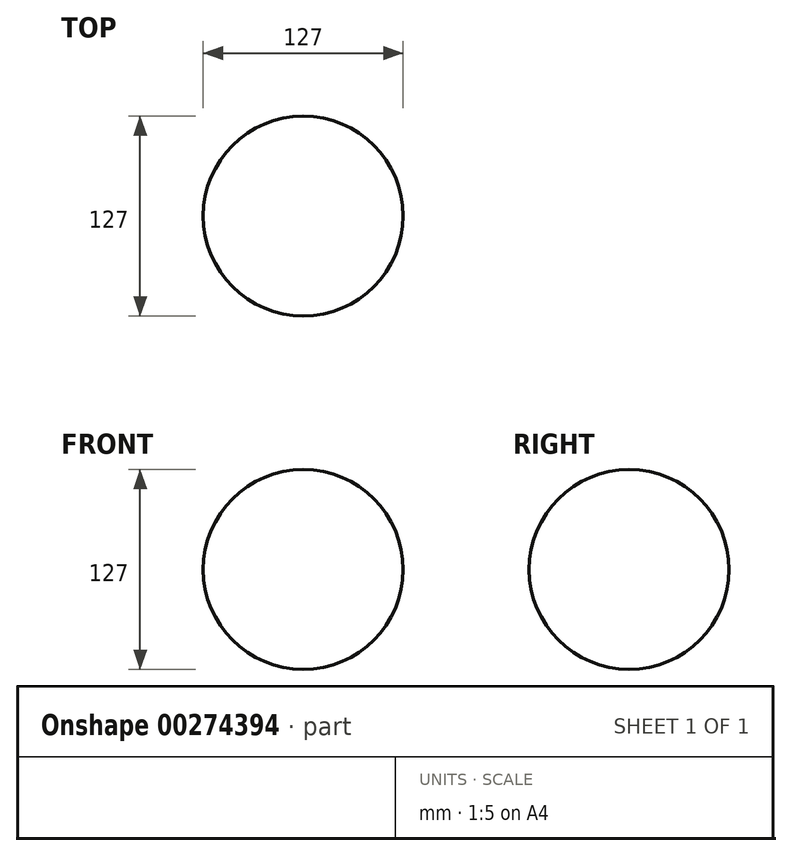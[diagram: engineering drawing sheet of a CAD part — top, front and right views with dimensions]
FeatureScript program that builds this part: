
annotation { "Feature Type Name" : "Feature", "Feature Type Description" : "" }
export const myFeature = defineFeature(function(context is Context, id is Id, definition is map)
    precondition{}
    {
        {
            var Q0;
            Q0=qCreatedBy(makeId("Front.planeOp"),FACE);
            var sketch = newSketch(context, id + "F0", { "sketchPlane" : qUnion([Q0])});
            skArc(sketch, "E0", {"start": v(0, -63.5) * mm, "mid": v(63.5, 0) * mm, "end": v(0, 63.5) * mm});
            skLineSegment(sketch, "E1", {"start": v(0, 63.5) * mm, "end": v(0, -63.5) * mm});
            skSolve(sketch);
        }
        {
            var Q0;
            Q0=makeQuery(id+"F0.imprint","IMPRINT",FACE,{"disambiguationData":[TD([[makeQuery(id+"F0.imprint","IMPRINT",EDGE,{"derivedFrom":sQuery(id+"F0.wireOp",EDGE,"E0")}),1.0]])]});
            var Q1;
            Q1=sQuery(id+"F0.wireOp",EDGE,"E1");
            revolve(context, id + "F1", {"entities" : qUnion([Q0]), "axis" : qUnion([Q1]), "revolveType" : RevolveType.FULL});
        }
        {
            var Q0;
            Q0=makeQuery(id+"F1.opRevolve","SWEPT_BODY",BODY,{"disambiguationData":[OSD([sQuery(id+"F0.wireOp",EDGE,"E0"),sQuery(id+"F0.wireOp",EDGE,"E1")])]});
            transform(context, id + "F2", {"entities" : qUnion([Q0]), "transformType" : TransformType.TRANSLATION_3D, "dx" : 0 * mm, "dy" : 0 * mm, "dz" : 0 * mm, "makeCopy" : false});
        }
    });
